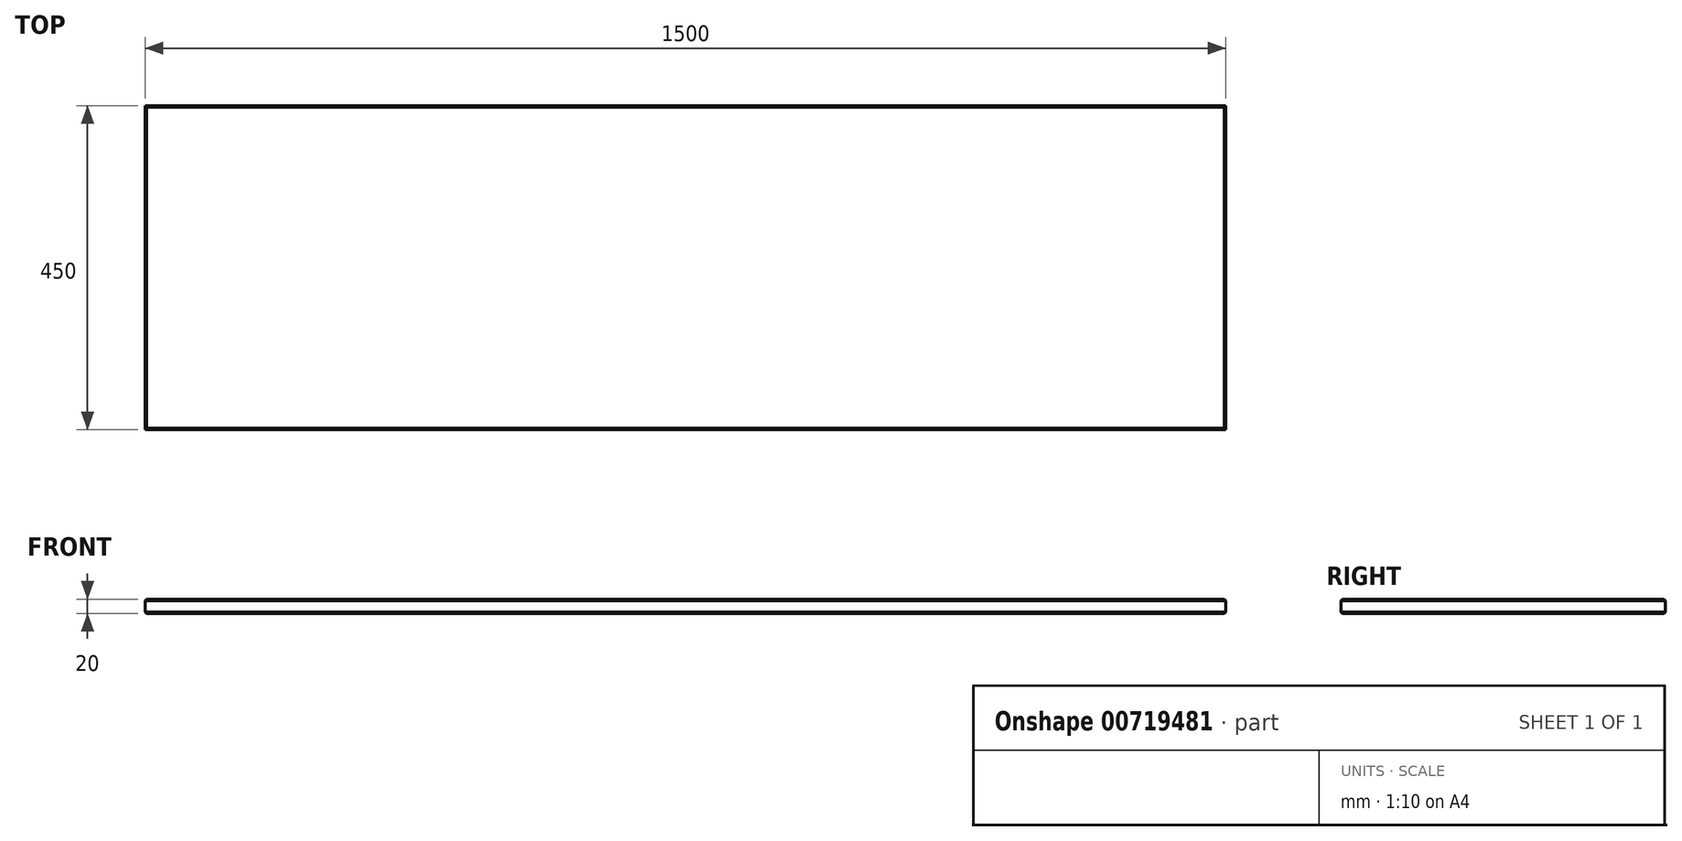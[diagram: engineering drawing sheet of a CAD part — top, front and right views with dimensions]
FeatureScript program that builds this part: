
annotation { "Feature Type Name" : "Feature", "Feature Type Description" : "" }
export const myFeature = defineFeature(function(context is Context, id is Id, definition is map)
    precondition{}
    {
        {
            var Q0;
            Q0=qCreatedBy(makeId("Top.planeOp"),FACE);
            var sketch = newSketch(context, id + "F0", { "sketchPlane" : qUnion([Q0])});
            skLineSegment(sketch, "E0.bottom", {"start": v(750, 225) * mm, "end": v(-750, 225) * mm});
            skLineSegment(sketch, "E0.top", {"start": v(750, -225) * mm, "end": v(-750, -225) * mm});
            skLineSegment(sketch, "E0.left", {"start": v(750, 225) * mm, "end": v(750, -225) * mm});
            skLineSegment(sketch, "E0.right", {"start": v(-750, 225) * mm, "end": v(-750, -225) * mm});
            skPoint(sketch, "E0.middle", {"position": v(0, 0) * mm});
            skSolve(sketch);
        }
        {
            var Q0;
            Q0=makeQuery(id+"F0.imprint","IMPRINT",FACE,{"disambiguationData":[TD([[makeQuery(id+"F0.imprint","IMPRINT",EDGE,{"derivedFrom":sQuery(id+"F0.wireOp",EDGE,"E0.bottom")}),1.0]])]});
            extrude(context, id + "F1", {"entities" : qUnion([Q0]), "depth" : 20 * mm, "offsetDistance" : 25 * mm});
        }
        {
            var Q0;
            Q0=makeQuery(id+"F1.opExtrude","CAP_FACE",FACE,{"disambiguationData":[OSD([sQuery(id+"F0.wireOp",EDGE,"E0.bottom"),sQuery(id+"F0.wireOp",EDGE,"E0.top"),sQuery(id+"F0.wireOp",EDGE,"E0.left"),sQuery(id+"F0.wireOp",EDGE,"E0.right")])],"isStart":false});
            var Q1;
            Q1=makeQuery(id+"F1.opExtrude","CAP_FACE",FACE,{"disambiguationData":[OSD([sQuery(id+"F0.wireOp",EDGE,"E0.bottom"),sQuery(id+"F0.wireOp",EDGE,"E0.top"),sQuery(id+"F0.wireOp",EDGE,"E0.left"),sQuery(id+"F0.wireOp",EDGE,"E0.right")])],"isStart":true});
            chamfer(context, id + "F2", {"entities" : qUnion([Q0, Q1]), "width" : 2 * mm, "tangentPropagation" : true});
        }
    });
